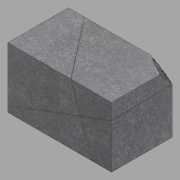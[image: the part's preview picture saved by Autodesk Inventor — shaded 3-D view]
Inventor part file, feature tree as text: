
AUTODESK INVENTOR PART (.ipt)
format: ipt  version: 2022.1 (Build 261234020, 234B)  size: 1,094,656 bytes
history: native  units: in
note: dims shown in document units (in); Inventor stores cm internally (conversion verified against a paired STEP export)
features: other x3, sketch x2, loft x1
ambient origin geometry x8: Origin, YZ Plane, XZ Plane, XY Plane, X Axis, Y Axis, Z Axis, Center Point
bodies: Solid1 (feature_tree)
feature tree (6):
  other  "4th.ipt"
  loft  "Loft1"
  other  "Solid1::4th.ipt"
  other  "TaggingFeature1"
  sketch  "Sketch1"  dims[d0=0.3937in d1=0.0in d2=90.0deg]
  sketch  "Sketch2"  dims[d3=0.0in d4=90.0deg]
